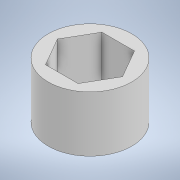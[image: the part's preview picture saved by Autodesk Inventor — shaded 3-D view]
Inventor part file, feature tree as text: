
AUTODESK INVENTOR PART (.ipt)
format: ipt  version: 2022.3 (Build 263350000, 350)  size: 99,328 bytes
history: native  units: in
note: dims shown in document units (in); Inventor stores cm internally (conversion verified against a paired STEP export)
features: extrude x1, sketch x1
ambient origin geometry x8: Origin, YZ Plane, XZ Plane, XY Plane, X Axis, Y Axis, Z Axis, Center Point
bodies: Solid1 (feature_tree)
feature tree (2):
  extrude  "Extrusion1"  Depth=0.5in
  sketch  "Sketch1"  dims[d0=0.507in d1=0.75in d2=0.5in d3=0.0in]
